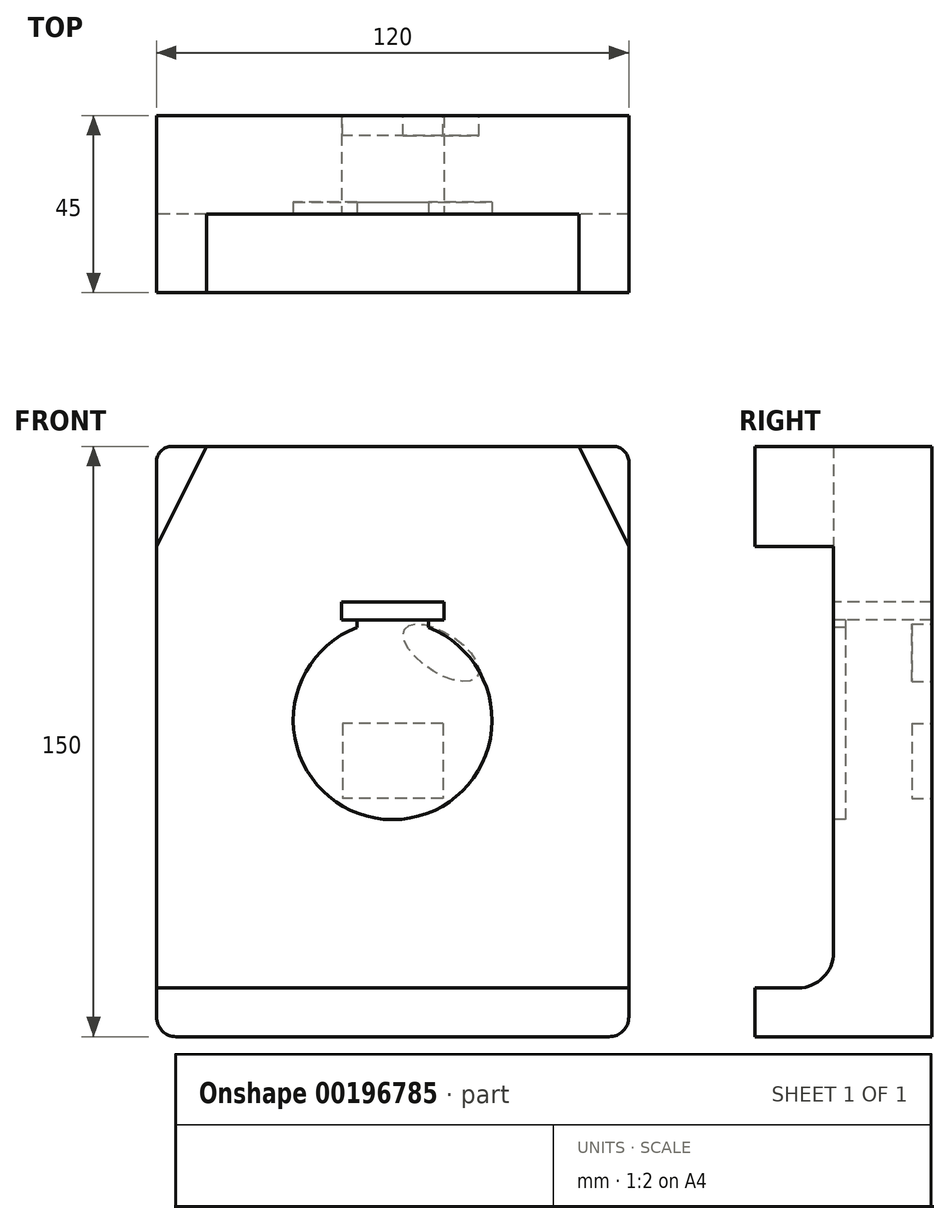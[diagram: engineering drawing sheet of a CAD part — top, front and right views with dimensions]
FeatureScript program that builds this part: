
annotation { "Feature Type Name" : "Feature", "Feature Type Description" : "" }
export const myFeature = defineFeature(function(context is Context, id is Id, definition is map)
    precondition{}
    {
        {
            var Q0;
            Q0=qCreatedBy(makeId("Front.planeOp"),FACE);
            var sketch = newSketch(context, id + "F0", { "sketchPlane" : qUnion([Q0])});
            skLineSegment(sketch, "E0.bottom", {"start": v(60, 80) * mm, "end": v(-60, 80) * mm});
            skLineSegment(sketch, "E0.top", {"start": v(60, -70) * mm, "end": v(-60, -70) * mm});
            skLineSegment(sketch, "E0.left", {"start": v(60, 80) * mm, "end": v(60, -70) * mm});
            skLineSegment(sketch, "E0.right", {"start": v(-60, 80) * mm, "end": v(-60, -70) * mm});
            skSolve(sketch);
        }
        {
            var Q0;
            Q0=makeQuery(id+"F0.imprint","IMPRINT",FACE,{"disambiguationData":[TD([[makeQuery(id+"F0.imprint","IMPRINT",EDGE,{"derivedFrom":sQuery(id+"F0.wireOp",EDGE,"E0.bottom")}),1.0]])]});
            extrude(context, id + "F1", {"entities" : qUnion([Q0]), "depth" : 45 * mm});
        }
        {
            var Q0;
            Q0=makeQuery(id+"F1.opExtrude","CAP_FACE",FACE,{"disambiguationData":[OSD([sQuery(id+"F0.wireOp",EDGE,"E0.bottom"),sQuery(id+"F0.wireOp",EDGE,"E0.top"),sQuery(id+"F0.wireOp",EDGE,"E0.left"),sQuery(id+"F0.wireOp",EDGE,"E0.right")])],"isStart":false});
            var sketch = newSketch(context, id + "F2", { "sketchPlane" : qUnion([Q0])});
            skLineSegment(sketch, "E1.0.0", {"start": v(60, -70) * mm, "end": v(60, 80) * mm});
            skLineSegment(sketch, "E1.0.1", {"start": v(60, 80) * mm, "end": v(-60, 80) * mm});
            skLineSegment(sketch, "E1.0.2", {"start": v(-60, 80) * mm, "end": v(-60, -70) * mm});
            skLineSegment(sketch, "E1.0.3", {"start": v(-60, -70) * mm, "end": v(60, -70) * mm});
            skLineSegment(sketch, "E2", {"start": v(-47.3, 80) * mm, "end": v(-60, 54.6) * mm});
            skLineSegment(sketch, "E3", {"start": v(-60, 54.6) * mm, "end": v(-60, -57.6) * mm});
            skLineSegment(sketch, "E4", {"start": v(-60, -57.6) * mm, "end": v(60, -57.6) * mm});
            skLineSegment(sketch, "E5", {"start": v(60, -57.6) * mm, "end": v(60, 54.6) * mm});
            skLineSegment(sketch, "E6", {"start": v(60, 54.6) * mm, "end": v(47.3, 80) * mm});
            skSolve(sketch);
        }
        {
            var Q0;
            {var subQ0=sQuery(id+"F2.wireOp",EDGE,"E2");Q0=makeQuery(id+"F2.imprint","IMPRINT",FACE,{"disambiguationData":[TD([[makeQuery(id+"F2.imprint","IMPRINT",EDGE,{"derivedFrom":subQ0}),1.0]])]});}
            extrude(context, id + "F3", {"entities" : qUnion([Q0]), "operationType" : NewBodyOperationType.REMOVE, "oppositeDirection" : true, "depth" : 20 * mm});
        }
        {
            var Q0;
            Q0=makeQuery(id+"F3.boolean.opBoolean","COPY",EDGE,{"derivedFrom":makeQuery(id+"F3.opExtrude","CAP_EDGE",EDGE,{"disambiguationData":[OSD([sQuery(id+"F2.wireOp",EDGE,"E4")])],"isStart":false})});
            fillet(context, id + "F4", {"entities" : qUnion([Q0]), "radius" : 9 * mm, "tangentPropagation" : true, "allowEdgeOverflow" : false});
        }
        {
            var Q0;
            Q0=makeQuery(id+"F3.boolean.opBoolean","COPY",EDGE,{"derivedFrom":makeQuery(id+"F3.opExtrude","SWEPT_EDGE",EDGE,{"disambiguationData":[OSD([sQuery(id+"F2.wireOp",EDGE,"E1.0.0"),sQuery(id+"F2.wireOp",EDGE,"E5"),sQuery(id+"F2.wireOp",EDGE,"E6")])]})});
            var Q1;
            Q1=makeQuery(id+"F3.boolean.opBoolean","COPY",EDGE,{"derivedFrom":makeQuery(id+"F3.opExtrude","SWEPT_EDGE",EDGE,{"disambiguationData":[OSD([sQuery(id+"F2.wireOp",EDGE,"E1.0.2"),sQuery(id+"F2.wireOp",EDGE,"E2"),sQuery(id+"F2.wireOp",EDGE,"E3")])]})});
            var Q2;
            Q2=makeQuery(id+"F3.boolean.opBoolean","COPY",EDGE,{"derivedFrom":makeQuery(id+"F3.opExtrude","SWEPT_EDGE",EDGE,{"disambiguationData":[OSD([sQuery(id+"F2.wireOp",EDGE,"E1.0.1"),sQuery(id+"F2.wireOp",EDGE,"E2")])]})});
            var Q3;
            Q3=makeQuery(id+"F1.opExtrude","SWEPT_EDGE",EDGE,{"disambiguationData":[OSD([sQuery(id+"F0.wireOp",EDGE,"E0.bottom"),sQuery(id+"F0.wireOp",EDGE,"E0.right")])]});
            var Q4;
            Q4=makeQuery(id+"F1.opExtrude","SWEPT_EDGE",EDGE,{"disambiguationData":[OSD([sQuery(id+"F0.wireOp",EDGE,"E0.bottom"),sQuery(id+"F0.wireOp",EDGE,"E0.left")])]});
            var Q5;
            Q5=makeQuery(id+"F3.boolean.opBoolean","COPY",EDGE,{"derivedFrom":makeQuery(id+"F3.opExtrude","SWEPT_EDGE",EDGE,{"disambiguationData":[OSD([sQuery(id+"F2.wireOp",EDGE,"E1.0.1"),sQuery(id+"F2.wireOp",EDGE,"E6")])]})});
            fillet(context, id + "F5", {"entities" : qUnion([Q0, Q1, Q2, Q3, Q4, Q5]), "radius" : 4 * mm, "tangentPropagation" : true, "allowEdgeOverflow" : false});
        }
        {
            var Q0;
            Q0=makeQuery(id+"F1.opExtrude","SWEPT_EDGE",EDGE,{"disambiguationData":[OSD([sQuery(id+"F0.wireOp",EDGE,"E0.top"),sQuery(id+"F0.wireOp",EDGE,"E0.left")])]});
            var Q1;
            Q1=makeQuery(id+"F1.opExtrude","SWEPT_EDGE",EDGE,{"disambiguationData":[OSD([sQuery(id+"F0.wireOp",EDGE,"E0.top"),sQuery(id+"F0.wireOp",EDGE,"E0.right")])]});
            fillet(context, id + "F6", {"entities" : qUnion([Q0, Q1]), "radius" : 5 * mm, "tangentPropagation" : true, "allowEdgeOverflow" : false});
        }
        {
            var Q0;
            Q0=makeQuery(id+"F1.opExtrude","CAP_FACE",FACE,{"disambiguationData":[OSD([sQuery(id+"F0.wireOp",EDGE,"E0.bottom"),sQuery(id+"F0.wireOp",EDGE,"E0.top"),sQuery(id+"F0.wireOp",EDGE,"E0.left"),sQuery(id+"F0.wireOp",EDGE,"E0.right")])],"isStart":true});
            var sketch = newSketch(context, id + "F7", { "sketchPlane" : qUnion([Q0])});
            skLineSegment(sketch, "E7.bottom", {"start": v(-12.8, 9.53) * mm, "end": v(12.7, 9.53) * mm});
            skLineSegment(sketch, "E7.top", {"start": v(-12.8, -9.53) * mm, "end": v(12.7, -9.53) * mm});
            skLineSegment(sketch, "E7.left", {"start": v(-12.8, 9.52) * mm, "end": v(-12.8, -9.53) * mm});
            skLineSegment(sketch, "E7.right", {"start": v(12.7, 9.53) * mm, "end": v(12.7, -9.53) * mm});
            skEllipse(sketch, "E8", {"center": v(-12.3, 27.53) * mm, "majorRadius": 11 * mm, "minorRadius": 5 * mm, "majorAxis": v(0.84, 0.54)});
            skLineSegment(sketch, "E9", {"start": v(-21.53, 21.53) * mm, "end": v(-3.07, 33.52) * mm, "construction": true});
            skSolve(sketch);
        }
        {
            var Q0;
            Q0 = qSketchRegion(id + "F7", true);
            extrude(context, id + "F8", {"entities" : qUnion([Q0]), "operationType" : NewBodyOperationType.REMOVE, "oppositeDirection" : true, "depth" : 5.1 * mm});
        }
        {
            var Q0;
            Q0=makeQuery(id+"F3.boolean.opBoolean","COPY",FACE,{"derivedFrom":makeQuery(id+"F3.opExtrude","CAP_FACE",FACE,{"disambiguationData":[OSD([sQuery(id+"F2.wireOp",EDGE,"E1.0.1"),sQuery(id+"F2.wireOp",EDGE,"E2"),sQuery(id+"F2.wireOp",EDGE,"E3"),sQuery(id+"F2.wireOp",EDGE,"E4"),sQuery(id+"F2.wireOp",EDGE,"E5"),sQuery(id+"F2.wireOp",EDGE,"E6")])],"isStart":false})});
            var sketch = newSketch(context, id + "F9", { "sketchPlane" : qUnion([Q0])});
            skArc(sketch, "E10", {"start": v(-9.05, 33.97) * mm, "mid": v(0, -14.85) * mm, "end": v(9.05, 33.97) * mm});
            skLineSegment(sketch, "E11.bottom", {"start": v(-13.05, 40.4) * mm, "end": v(13.05, 40.4) * mm});
            skLineSegment(sketch, "E11.top", {"start": v(-13.05, 35.9) * mm, "end": v(-9.05, 35.9) * mm});
            skLineSegment(sketch, "E11.left", {"start": v(-13.05, 40.4) * mm, "end": v(-13.05, 35.9) * mm});
            skLineSegment(sketch, "E11.right", {"start": v(13.05, 40.4) * mm, "end": v(13.05, 35.9) * mm});
            skLineSegment(sketch, "E12", {"start": v(-9.05, 35.9) * mm, "end": v(-9.05, 33.97) * mm});
            skLineSegment(sketch, "E13", {"start": v(9.05, 35.9) * mm, "end": v(9.05, 33.97) * mm});
            skLineSegment(sketch, "E14.trimOffspring", {"start": v(9.05, 35.9) * mm, "end": v(13.05, 35.9) * mm});
            skSolve(sketch);
        }
        {
            var Q0;
            Q0 = qSketchRegion(id + "F9", true);
            extrude(context, id + "F10", {"entities" : qUnion([Q0]), "operationType" : NewBodyOperationType.REMOVE, "oppositeDirection" : true, "depth" : 3 * mm});
        }
        {
            var Q0;
            Q0=makeQuery(id+"F10.boolean.opBoolean","COPY",FACE,{"derivedFrom":makeQuery(id+"F10.opExtrude","CAP_FACE",FACE,{"disambiguationData":[OSD([sQuery(id+"F9.wireOp",EDGE,"E10"),sQuery(id+"F9.wireOp",EDGE,"E11.bottom"),sQuery(id+"F9.wireOp",EDGE,"E11.top"),sQuery(id+"F9.wireOp",EDGE,"E11.left"),sQuery(id+"F9.wireOp",EDGE,"E11.right"),sQuery(id+"F9.wireOp",EDGE,"E12"),sQuery(id+"F9.wireOp",EDGE,"E13"),sQuery(id+"F9.wireOp",EDGE,"E14.trimOffspring")])],"isStart":false})});
            var sketch = newSketch(context, id + "F11", { "sketchPlane" : qUnion([Q0])});
            skLineSegment(sketch, "E15.0", {"start": v(-13.05, 40.4) * mm, "end": v(13.05, 40.4) * mm});
            skPoint(sketch, "E16.0", {"position": v(13.05, 38.15) * mm});
            skLineSegment(sketch, "E17.0", {"start": v(13.05, 40.4) * mm, "end": v(13.05, 35.9) * mm});
            skLineSegment(sketch, "E18.0", {"start": v(9.05, 35.9) * mm, "end": v(13.05, 35.9) * mm});
            skLineSegment(sketch, "E19.0", {"start": v(-13.05, 40.4) * mm, "end": v(-13.05, 35.9) * mm});
            skLineSegment(sketch, "E20.0", {"start": v(-13.05, 35.9) * mm, "end": v(-9.05, 35.9) * mm});
            skLineSegment(sketch, "E21", {"start": v(-9.05, 35.9) * mm, "end": v(9.05, 35.9) * mm});
            skSolve(sketch);
        }
        {
            var Q0;
            Q0 = qSketchRegion(id + "F11", true);
            extrude(context, id + "F12", {"entities" : qUnion([Q0]), "operationType" : NewBodyOperationType.REMOVE, "endBound" : BoundingType.THROUGH_ALL, "oppositeDirection" : true, "depth" : 25 * mm});
        }
    });
